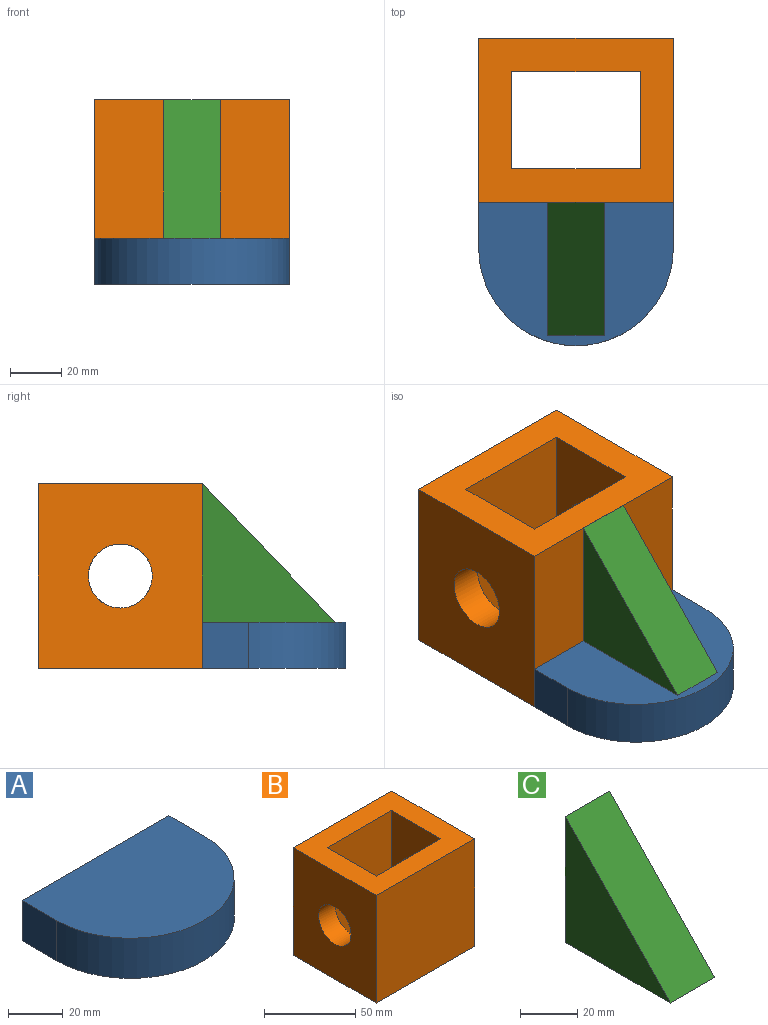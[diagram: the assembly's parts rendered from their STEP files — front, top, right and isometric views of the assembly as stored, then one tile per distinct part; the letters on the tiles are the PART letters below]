
ASSEMBLY  parts=3 mates=2
PART A: 6 faces, bbox 76x56x18 mm
  f0: cylinder r=38mm len=76mm, axis (0,0,-1), area 2148.8mm2, adj f1,f2,f3,f4
  f1: plane 76x56mm, normal (0,0,1), area 3636.2mm2, adj f0,f3,f4,f5
  f2: plane 76x56mm, normal (0,0,-1), area 3636.2mm2, adj f0,f3,f4,f5
  f3: plane 18x18mm, normal (-1,0,0), area 324mm2, adj f0,f1,f2,f5
  f4: plane 18x18mm, normal (1,0,0), area 324mm2, adj f0,f1,f2,f5
  f5: plane 76x18mm, normal (0,1,0), area 1368mm2, adj f1,f2,f3,f4
PART B: 12 faces, bbox 76x64x72 mm
  f0: plane 76x64mm, normal (0,0,-1), area 2964mm2, adj f3,f4,f6,f7,f8,f9,f10,f11
  f1: plane 76x64mm, normal (0,0,1), area 2964mm2, adj f3,f4,f6,f7,f8,f9,f10,f11
  f2: cylinder r=12.5mm len=25mm, axis (1,0,0), area 1021mm2, adj f7,f9
  f3: plane 76x72mm, normal (0,-1,0), area 5472mm2, adj f0,f1,f6,f7
  f4: plane 76x72mm, normal (0,1,0), area 5472mm2, adj f0,f1,f6,f7
  f5: cylinder r=12.5mm len=25mm, axis (1,0,0), area 1021mm2, adj f6,f8
  f6: plane 72x64mm, normal (-1,0,0), area 4117.1mm2, adj f0,f1,f3,f4,f5
  f7: plane 72x64mm, normal (1,0,0), area 4117.1mm2, adj f0,f1,f2,f3,f4
  f8: plane 72x38mm, normal (1,0,0), area 2245.1mm2, adj f0,f1,f5,f10,f11
  f9: plane 72x38mm, normal (-1,0,0), area 2245.1mm2, adj f0,f1,f2,f10,f11
  f10: plane 72x50mm, normal (0,-1,0), area 3600mm2, adj f0,f1,f8,f9
  f11: plane 72x50mm, normal (0,1,0), area 3600mm2, adj f0,f1,f8,f9
PART C: 5 faces, bbox 22x52x54 mm
  f0: plane 52x22mm, normal (0,0,-1), area 1144mm2, adj f1,f2,f3,f4
  f1: plane 54x22mm, normal (0,1,0), area 1188mm2, adj f0,f2,f3,f4
  f2: plane 54x52mm, normal (0,-0.72,0.69), area 1649.3mm2, adj f0,f1,f3,f4
  f3: plane 54x52mm, normal (1,0,0), area 1404mm2, adj f0,f1,f2
  f4: plane 54x52mm, normal (-1,0,0), area 1404mm2, adj f0,f1,f2
PLACE A t=(-34.04,-16.54,10.75)mm
PLACE B t=(41.96,1.46,10.75)mm
PLACE C t=(-7.04,1.46,28.75)mm
MATE fastened A.f5 <-> B.f3  axis (0,1,0) through (3.96,1.46,10.75)mm
MATE fastened C.f1 <-> B.f3  axis (0,1,0) through (3.96,1.46,55.75)mm
